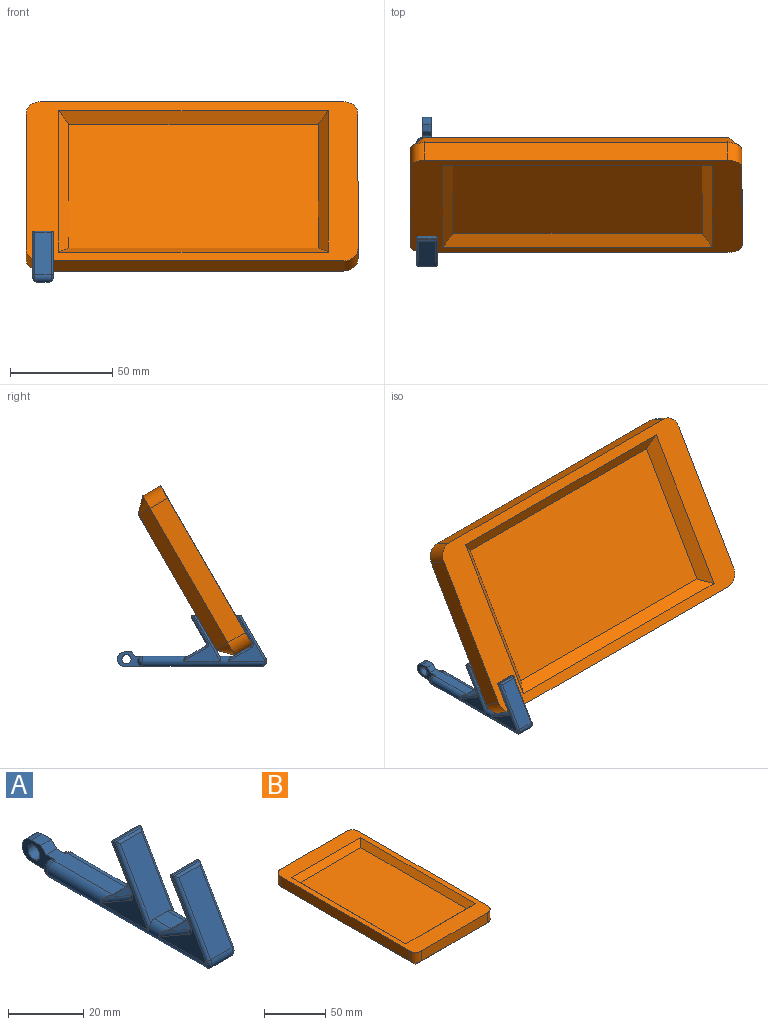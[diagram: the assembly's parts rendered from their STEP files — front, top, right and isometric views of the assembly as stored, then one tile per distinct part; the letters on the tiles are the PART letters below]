
ASSEMBLY  parts=2 mates=1
PART A: 64 faces, bbox 10x73.4x25.5 mm
  f0: plane 22.5x17.78mm, normal (-1,0,0), area 81.3mm2, adj f7,f20,f28,f29,f46,f49,f51,f53
  f1: plane 22.5x18.01mm, normal (1,0,0), area 81.3mm2, adj f6,f22,f31,f32,f33,f34,f59
  f2: plane 25.45x5mm, normal (0,0,1), area 123.8mm2, adj f15,f16,f17,f18,f20,f22,f41,f63
  f3: plane 67.17x5mm, normal (0,0,-1), area 326.8mm2, adj f15,f16,f17,f18,f20,f21,f22,f62
  f4: plane 22.5x18.01mm, normal (-1,0,0), area 81.3mm2, adj f6,f20,f33,f36,f38,f40,f57
  f5: plane 22.5x17.78mm, normal (1,0,0), area 81.3mm2, adj f7,f22,f25,f26,f44,f45,f46,f47
  f6: plane 10.01x0.7mm, normal (0,0,1), area 6.9mm2, adj f1,f4,f33,f57,f58,f59
  f7: plane 10.01x0.7mm, normal (0,0,1), area 6.9mm2, adj f0,f5,f26,f27,f28,f46
  f8: plane 8.78x8mm, normal (0,0.5,0.87), area 76.4mm2, adj f34,f35,f39,f40,f41,f43
  f9: plane 12.27x8mm, normal (0,0.87,-0.5), area 113.3mm2, adj f31,f33,f35,f36
  f10: plane 20.75x11.98mm, normal (0,-0.87,0.5), area 191.7mm2, adj f21,f26,f27,f28
  f11: plane 8.78x8mm, normal (0,0.5,0.87), area 76.4mm2, adj f47,f48,f52,f53,f54,f56
  f12: plane 6.34x5mm, normal (0,0,1), area 31.7mm2, adj f14,f20,f22,f54
  f13: plane 12.27x8mm, normal (0,0.87,-0.5), area 113.3mm2, adj f44,f46,f48,f49
  f14: plane 20x11.55mm, normal (0,-0.87,0.5), area 180.7mm2, adj f12,f20,f22,f57,f58,f59
  f15: plane 12.5x7mm, normal (1,0,0), area 47.5mm2, adj f2,f3,f18,f60,f61,f62,f63
  f16: plane 12.5x7mm, normal (-1,0,0), area 47.5mm2, adj f2,f3,f17,f60,f61,f62,f63
  f17: cylinder r=2.5mm len=5mm, axis (-1,0,0), area 3.9mm2, adj f2,f3,f16,f19
  f18: cylinder r=2.5mm len=5mm, axis (-1,0,0), area 3.9mm2, adj f2,f3,f15,f23
  f19: sphere r=2.5mm, area 19.6mm2, adj f17,f20
  f20: cylinder r=2.5mm len=59.67mm, axis (0,1,0), area 333.5mm2, adj f0,f2,f3,f4,f12,f14,f19,f30
  f21: cylinder r=2.5mm len=8mm, axis (-1,0,0), area 37.6mm2, adj f3,f10,f24,f25,f29,f30
  f22: cylinder r=2.5mm len=59.67mm, axis (0,-1,0), area 333.5mm2, adj f1,f2,f3,f5,f12,f14,f23,f24
  f23: sphere r=2.5mm, area 19.6mm2, adj f18,f22
  f24: bspline ~2.95x2.5mm, area 4.2mm2, adj f21,f22,f25
  f25: torus R=1.5mm, axis (-1,0,0), area 1.8mm2, adj f5,f21,f24,f26
  f26: cylinder r=1mm len=22.25mm, axis (0,-0.5,-0.87), area 38.7mm2, adj f5,f7,f10,f25,f27
  f27: cylinder r=1mm len=9.73mm, axis (1,0,0), area 9.4mm2, adj f7,f10,f26,f28
  f28: cylinder r=1mm len=22.25mm, axis (0,0.5,0.87), area 38.7mm2, adj f0,f7,f10,f27,f29
  f29: torus R=1.5mm, axis (-1,0,0), area 1.8mm2, adj f0,f21,f28,f30
  f30: bspline ~2.95x2.5mm, area 4.2mm2, adj f20,f21,f29
  f31: cylinder r=1mm len=13.63mm, axis (0,0.5,0.87), area 23.3mm2, adj f1,f9,f32,f33
  f32: torus R=2mm, axis (-1,0,0), area 3.4mm2, adj f1,f31,f34,f35
  f33: cylinder r=1mm len=10mm, axis (-1,0,0), area 19.8mm2, adj f1,f4,f6,f9,f31,f36
  f34: cylinder r=1mm len=11.76mm, axis (0,-0.87,0.5), area 18.2mm2, adj f1,f8,f32,f37
  f35: cylinder r=1mm len=8mm, axis (1,0,0), area 12.6mm2, adj f8,f9,f32,f38
  f36: cylinder r=1mm len=13.63mm, axis (0,-0.5,-0.87), area 23.3mm2, adj f4,f9,f33,f38
  f37: bspline ~2.56x2.53mm, area 1.2mm2, adj f22,f34,f39
  f38: torus R=2mm, axis (-1,0,0), area 3.4mm2, adj f4,f35,f36,f40
  f39: bspline ~1.5x1.09mm, area 0.9mm2, adj f8,f22,f37,f41
  f40: cylinder r=1mm len=11.76mm, axis (0,0.87,-0.5), area 18.2mm2, adj f4,f8,f38,f42
  f41: cylinder r=1mm len=5mm, axis (1,0,0), area 2.6mm2, adj f2,f8,f39,f43
  f42: bspline ~2.56x2.53mm, area 1.2mm2, adj f20,f40,f43
  f43: bspline ~1.5x1.09mm, area 0.9mm2, adj f8,f20,f41,f42
  f44: cylinder r=1mm len=13.63mm, axis (0,0.5,0.87), area 23.3mm2, adj f5,f13,f45,f46
  f45: torus R=2mm, axis (-1,0,0), area 3.4mm2, adj f5,f44,f47,f48
  f46: cylinder r=1mm len=10mm, axis (-1,0,0), area 19.8mm2, adj f0,f5,f7,f13,f44,f49
  f47: cylinder r=1mm len=11.76mm, axis (0,-0.87,0.5), area 18.2mm2, adj f5,f11,f45,f50
  f48: cylinder r=1mm len=8mm, axis (-1,0,0), area 12.6mm2, adj f11,f13,f45,f51
  f49: cylinder r=1mm len=13.63mm, axis (0,-0.5,-0.87), area 23.3mm2, adj f0,f13,f46,f51
  f50: bspline ~2.56x2.53mm, area 1.2mm2, adj f22,f47,f52
  f51: torus R=2mm, axis (-1,0,0), area 3.4mm2, adj f0,f48,f49,f53
  f52: bspline ~1.88x1.44mm, area 0.9mm2, adj f11,f22,f50,f54
  f53: cylinder r=1mm len=11.76mm, axis (0,0.87,-0.5), area 18.2mm2, adj f0,f11,f51,f55
  f54: cylinder r=1mm len=5mm, axis (1,0,0), area 2.6mm2, adj f11,f12,f52,f56
  f55: bspline ~2.56x2.53mm, area 1.2mm2, adj f20,f53,f56
  f56: bspline ~2.04x1.44mm, area 0.9mm2, adj f11,f20,f54,f55
  f57: cylinder r=1mm len=23mm, axis (0,0.5,0.87), area 38.6mm2, adj f4,f6,f14,f20,f58
  f58: cylinder r=1mm len=9.73mm, axis (1,0,0), area 9.4mm2, adj f6,f14,f57,f59
  f59: cylinder r=1mm len=23mm, axis (0,-0.5,-0.87), area 38.6mm2, adj f1,f6,f14,f22,f58
  f60: plane 4x3.5mm, normal (0,0,1), area 14mm2, adj f15,f16,f62,f63
  f61: cylinder r=2.25mm len=4.5mm, axis (-1,0,0), area 56.5mm2, adj f15,f16
  f62: cylinder r=3.5mm len=7mm, axis (-1,0,0), area 44mm2, adj f3,f15,f16,f60
  f63: plane 4x2mm, normal (0,-0.71,0.71), area 11.3mm2, adj f2,f15,f16,f60
PART B: 23 faces, bbox 90x162.6x16.5 mm
  f0: plane 162.6x90mm, normal (0,0,1), area 4023.9mm2, adj f1,f2,f3,f4,f6,f7,f8,f9
  f1: plane 76x10mm, normal (0,1,0), area 760mm2, adj f0,f6,f9,f18
  f2: plane 148.6x10mm, normal (-1,0,0), area 1486mm2, adj f0,f6,f7,f15
  f3: plane 76x10mm, normal (0,-1,0), area 760mm2, adj f0,f7,f8,f19
  f4: plane 148.6x10mm, normal (1,0,0), area 1486mm2, adj f0,f8,f9,f22
  f5: plane 149.6x77mm, normal (0,0,-1), area 11519mm2, adj f15,f16,f17,f18,f19,f20,f21,f22
  f6: cylinder r=7mm len=10mm, axis (0,0,1), area 110mm2, adj f0,f1,f2,f16
  f7: cylinder r=7mm len=10mm, axis (0,0,-1), area 110mm2, adj f0,f2,f3,f17
  f8: cylinder r=7mm len=10mm, axis (0,0,1), area 110mm2, adj f0,f3,f4,f21
  f9: cylinder r=7mm len=10mm, axis (0,0,-1), area 110mm2, adj f0,f1,f4,f20
  f10: plane 122.1x70mm, normal (0,0,1), area 8547mm2, adj f11,f12,f13,f14
  f11: plane 132.1x5mm, normal (0.71,0,0.71), area 898.7mm2, adj f0,f10,f12,f13
  f12: plane 80x5mm, normal (0,0.71,0.71), area 530.3mm2, adj f0,f10,f11,f14
  f13: plane 80x5mm, normal (0,-0.71,0.71), area 530.3mm2, adj f0,f10,f11,f14
  f14: plane 132.1x5mm, normal (-0.71,0,0.71), area 898.7mm2, adj f0,f10,f12,f13
  f15: plane 148.6x6.5mm, normal (-0.71,0,-0.71), area 1366mm2, adj f2,f5,f16,f17
  f16: cone r=0.5mm half-angle=45deg, axis (0,0,1), area 54.1mm2, adj f5,f6,f15,f18
  f17: cone r=0.5mm half-angle=45deg, axis (0,0,1), area 54.1mm2, adj f5,f7,f15,f19
  f18: plane 76x6.5mm, normal (0,0.71,-0.71), area 698.6mm2, adj f1,f5,f16,f20
  f19: plane 76x6.5mm, normal (0,-0.71,-0.71), area 698.6mm2, adj f3,f5,f17,f21
  f20: cone r=0.5mm half-angle=45deg, axis (0,0,1), area 54.1mm2, adj f5,f9,f18,f22
  f21: cone r=0.5mm half-angle=45deg, axis (0,0,1), area 54.1mm2, adj f5,f8,f19,f22
  f22: plane 148.6x6.5mm, normal (0.71,0,-0.71), area 1366mm2, adj f4,f5,f20,f21
PLACE A t=(-16.81,2.33,8.9)mm
PLACE B rot(axis=(0.45,0.45,-0.77),104.5deg) t=(56.19,10.41,50.1)mm
MATE fastened B.f4 <-> A.f11  axis (0,-0.5,-0.87) through (56.19,-22.05,16.88)mm
